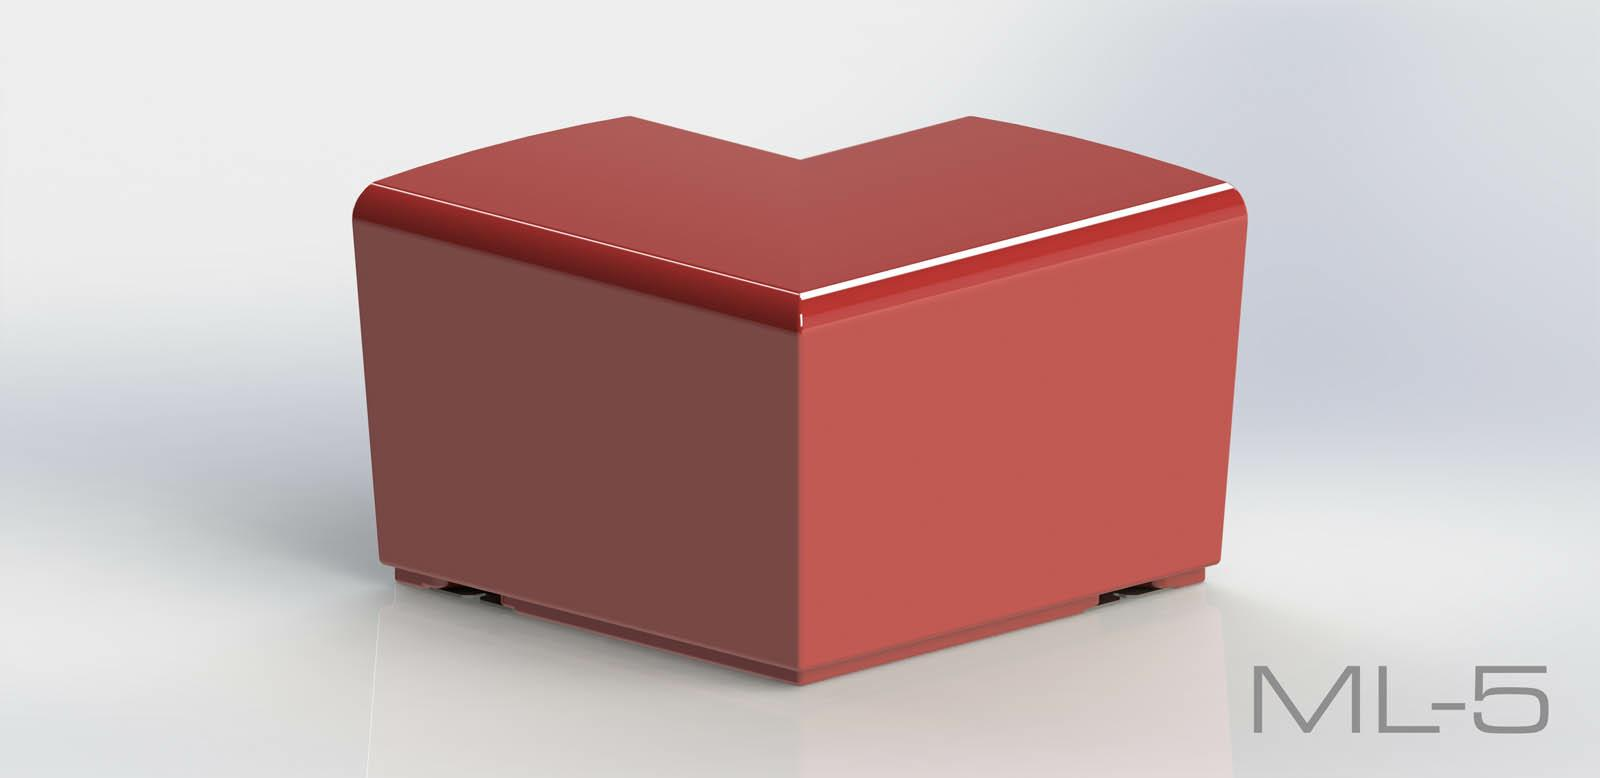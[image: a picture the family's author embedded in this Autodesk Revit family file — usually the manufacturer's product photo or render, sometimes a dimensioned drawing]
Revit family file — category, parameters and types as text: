
# Revit family: Modullaro ML 05
name_source: partatom
category: Furniture
revit_build: Autodesk Revit 2018 (Build: 20190510_1515(x64)
units: mm (PartAtom-declared; Revit-internal decimal feet)

## family parameters
Cut with Voids When Loaded = No
Host = Face
OmniClass Number = 23.40.10.11.14
OmniClass Title = Exterior Seating
Room Calculation Point = No
Shared = No

## types (1)
- Modullaro ML 05
    Default Elevation = 1219 mm
    Height = 500 mm  [stored 1.64042 ft]
    IfcExportAs = IfcFurnishingElement
    Length = 747 mm  [stored 2.45079 ft]
    Manufacturer = Astrini Design
    Material information = Colour choice from RAL colour standard. Customer may inquire about specific request regarding individual order.
    Model = Modullaro ML 05
    Operating temperature = -40°C to 80°C, ( -40°F to 176°F )
    Type Comments = Bench
    Type Image = ML-5.jpg
    URL = https://astrini-design.pl
    Weight (approximately) = 16.00 kg
    Width = 494 mm

note: [stored X ft] marks values corroborated as IEEE doubles in the binary element streams (Revit-internal decimal feet)
